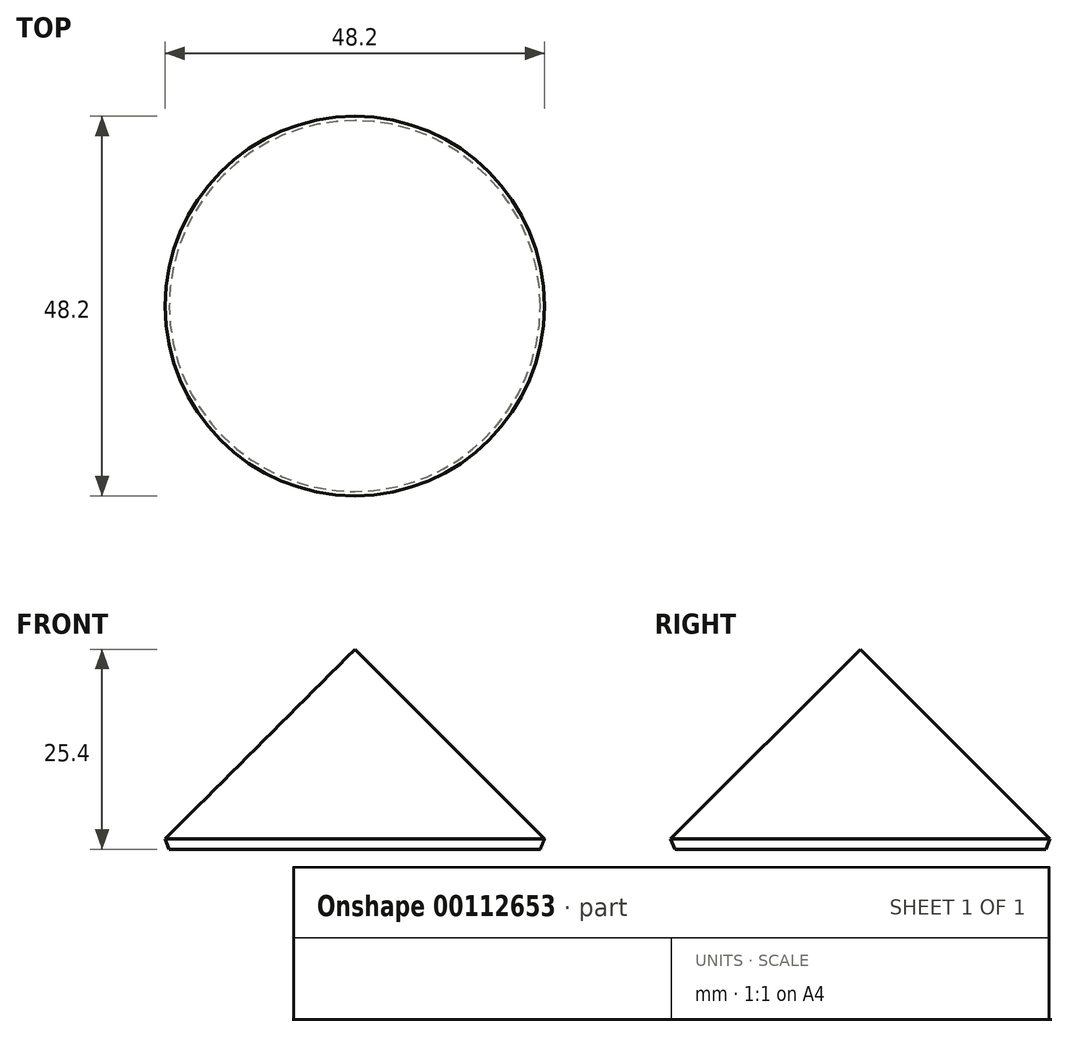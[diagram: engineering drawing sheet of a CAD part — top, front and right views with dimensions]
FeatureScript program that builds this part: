
annotation { "Feature Type Name" : "Feature", "Feature Type Description" : "" }
export const myFeature = defineFeature(function(context is Context, id is Id, definition is map)
    precondition{}
    {
        {
            var Q0;
            Q0=qCreatedBy(makeId("Top.planeOp"),FACE);
            var sketch = newSketch(context, id + "F0", { "sketchPlane" : qUnion([Q0])});
            skCircle(sketch, "E0", {"center": v(0, 0) * mm, "radius": 25.4 * mm});
            skSolve(sketch);
        }
        {
            var Q0;
            Q0 = qSketchRegion(id + "F0", true);
            extrude(context, id + "F1", {"entities" : qUnion([Q0]), "depth" : 25.4 * mm});
        }
        {
            var Q0;
            Q0=makeQuery(id+"F1.opExtrude","CAP_EDGE",EDGE,{"disambiguationData":[OSD([sQuery(id+"F0.wireOp",EDGE,"E0")])],"isStart":false});
            chamfer(context, id + "F2", {"entities" : qUnion([Q0]), "width" : 25.4 * mm, "tangentPropagation" : true});
        }
        {
            var Q0;
            {var subQ0=sQuery(id+"F0.wireOp",EDGE,"E0");Q0=makeQuery(id+"F2.opChamfer","BLEND_EDGE",EDGE,{"blendedFrom":[makeQuery(id+"F1.opExtrude","CAP_EDGE",EDGE,{"disambiguationData":[OSD([subQ0])],"isStart":false}),makeQuery(id+"F1.opExtrude","CAP_FACE",FACE,{"disambiguationData":[OSD([subQ0])],"isStart":true})],"blendedInto":[makeQuery(id+"F1.opExtrude","CAP_FACE",FACE,{"disambiguationData":[OSD([subQ0])],"isStart":true})]});}
            chamfer(context, id + "F3", {"entities" : qUnion([Q0]), "width" : 0.76 * mm, "tangentPropagation" : true});
        }
    });
